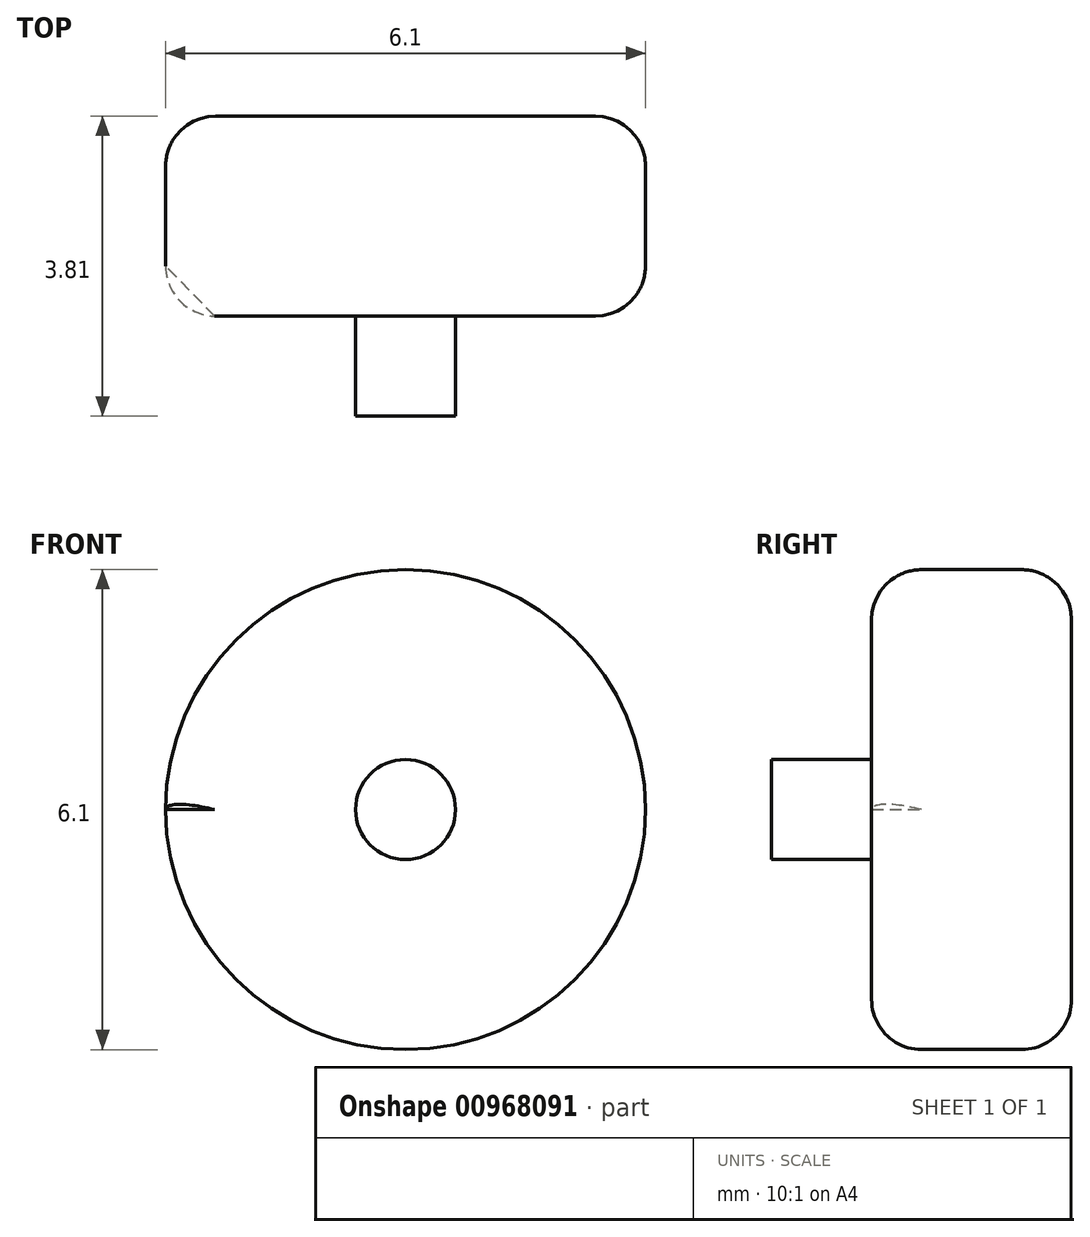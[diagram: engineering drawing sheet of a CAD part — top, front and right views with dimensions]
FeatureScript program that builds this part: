
annotation { "Feature Type Name" : "Feature", "Feature Type Description" : "" }
export const myFeature = defineFeature(function(context is Context, id is Id, definition is map)
    precondition{}
    {
        {
            var Q0;
            Q0=qCreatedBy(makeId("Front.planeOp"),FACE);
            cPlane(context, id + "F0", {"entities" : qUnion([Q0]), "cplaneType" : CPlaneType.OFFSET, "offset" : 1.27 * mm, "width" : 152.4 * mm, "height" : 152.4 * mm});
        }
        {
            var Q0;
            Q0=qCreatedBy(makeId("Front.planeOp"),FACE);
            var sketch = newSketch(context, id + "F1", { "sketchPlane" : qUnion([Q0])});
            skCircle(sketch, "E0", {"center": v(0, 0) * mm, "radius": 3.05 * mm});
            skSolve(sketch);
        }
        {
            var Q0;
            Q0 = qSketchRegion(id + "F1", true);
            extrude(context, id + "F2", {"entities" : qUnion([Q0]), "depth" : 2.54 * mm, "offsetDistance" : 25.4 * mm});
        }
        {
            var Q0;
            Q0=makeQuery(id+"F2.opExtrude","CAP_EDGE",EDGE,{"disambiguationData":[OSD([sQuery(id+"F1.wireOp",EDGE,"E0")])],"isStart":false});
            var Q1;
            Q1=makeQuery(id+"F2.opExtrude","CAP_EDGE",EDGE,{"disambiguationData":[OSD([sQuery(id+"F1.wireOp",EDGE,"E0")])],"isStart":true});
            fillet(context, id + "F3", {"entities" : qUnion([Q0, Q1]), "radius" : 0.64 * mm, "tangentPropagation" : true, "allowEdgeOverflow" : false});
        }
        {
            var Q0;
            Q0=qCreatedBy(makeId("Top.planeOp"),FACE);
            var sketch = newSketch(context, id + "F4", { "sketchPlane" : qUnion([Q0])});
            skLineSegment(sketch, "E1", {"start": v(-3.05, -1.9) * mm, "end": v(-2.43, -2.54) * mm});
            skLineSegment(sketch, "E2", {"start": v(-3.05, -1.9) * mm, "end": v(-3.43, -2.28) * mm});
            skLineSegment(sketch, "E3", {"start": v(-3.43, -2.28) * mm, "end": v(-2.8, -2.91) * mm});
            skLineSegment(sketch, "E4", {"start": v(-2.8, -2.91) * mm, "end": v(-2.43, -2.54) * mm});
            skSolve(sketch);
        }
        {
            var Q0;
            Q0 = qSketchRegion(id + "F4", true);
            extrude(context, id + "F5", {"entities" : qUnion([Q0]), "operationType" : NewBodyOperationType.REMOVE, "oppositeDirection" : true, "depth" : 25.4 * mm, "offsetDistance" : 25.4 * mm, "hasDraft" : true, "draftAngle" : 70 * degree, "draftPullDirection" : true, "hasSecondDirection" : true, "secondDirectionOppositeDirection" : false, "secondDirectionDepth" : 25.4 * mm, "hasSecondDirectionDraft" : true, "secondDirectionDraftAngle" : 70 * degree, "secondDirectionDraftPullDirection" : true});
        }
        {
            var Q0;
            Q0=makeQuery(id+"F2.opExtrude","CAP_FACE",FACE,{"disambiguationData":[OSD([sQuery(id+"F1.wireOp",EDGE,"E0")])],"isStart":false});
            var sketch = newSketch(context, id + "F6", { "sketchPlane" : qUnion([Q0])});
            skCircle(sketch, "E5", {"center": v(0, 0) * mm, "radius": 0.64 * mm});
            skSolve(sketch);
        }
        {
            var Q0;
            Q0 = qSketchRegion(id + "F6", true);
            extrude(context, id + "F7", {"entities" : qUnion([Q0]), "operationType" : NewBodyOperationType.ADD, "depth" : 1.27 * mm, "offsetDistance" : 25.4 * mm});
        }
    });
